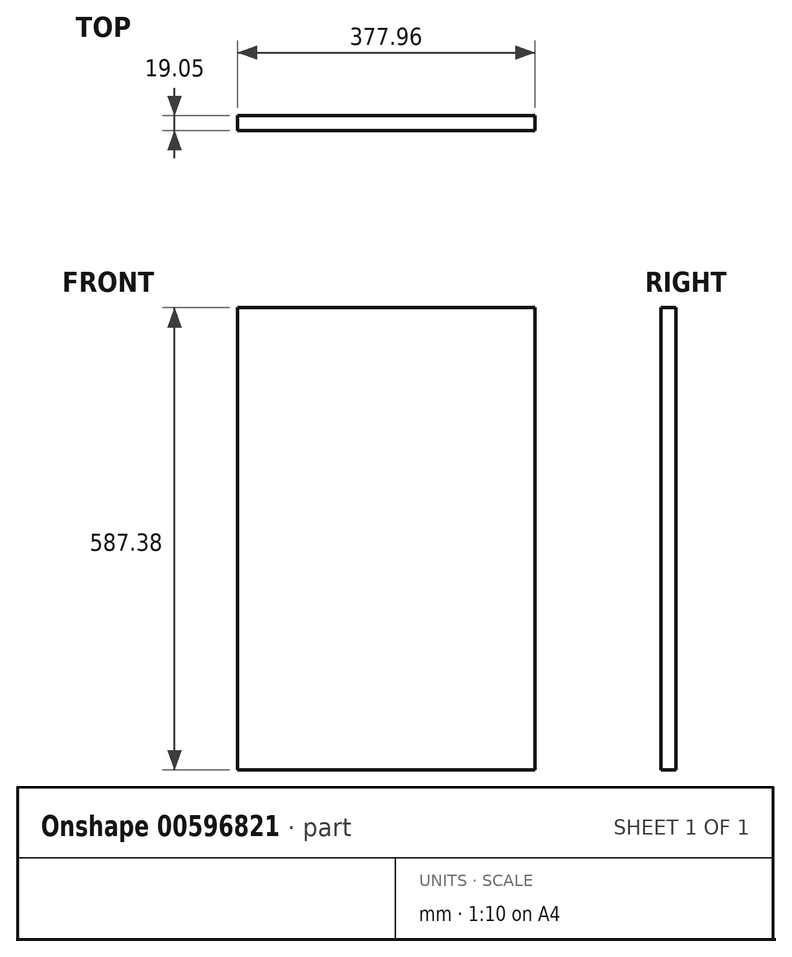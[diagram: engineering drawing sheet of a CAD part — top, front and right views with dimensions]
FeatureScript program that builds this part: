
annotation { "Feature Type Name" : "Feature", "Feature Type Description" : "" }
export const myFeature = defineFeature(function(context is Context, id is Id, definition is map)
    precondition{}
    {
        {
            var Q0;
            Q0=qCreatedBy(makeId("Front.planeOp"),FACE);
            var sketch = newSketch(context, id + "F0", { "sketchPlane" : qUnion([Q0])});
            skLineSegment(sketch, "E0.bottom", {"start": v(188.98, 293.69) * mm, "end": v(-188.98, 293.69) * mm});
            skLineSegment(sketch, "E0.top", {"start": v(188.98, -293.69) * mm, "end": v(-188.98, -293.69) * mm});
            skLineSegment(sketch, "E0.left", {"start": v(188.98, 293.69) * mm, "end": v(188.98, -293.69) * mm});
            skLineSegment(sketch, "E0.right", {"start": v(-188.98, 293.69) * mm, "end": v(-188.98, -293.69) * mm});
            skPoint(sketch, "E0.middle", {"position": v(0, 0) * mm});
            skSolve(sketch);
        }
        {
            var Q0;
            Q0=makeQuery(id+"F0.imprint","IMPRINT",FACE,{"disambiguationData":[TD([[makeQuery(id+"F0.imprint","IMPRINT",EDGE,{"derivedFrom":sQuery(id+"F0.wireOp",EDGE,"E0.bottom")}),1.0]])]});
            extrude(context, id + "F1", {"entities" : qUnion([Q0]), "depth" : 19.05 * mm, "offsetDistance" : 25.4 * mm});
        }
    });
